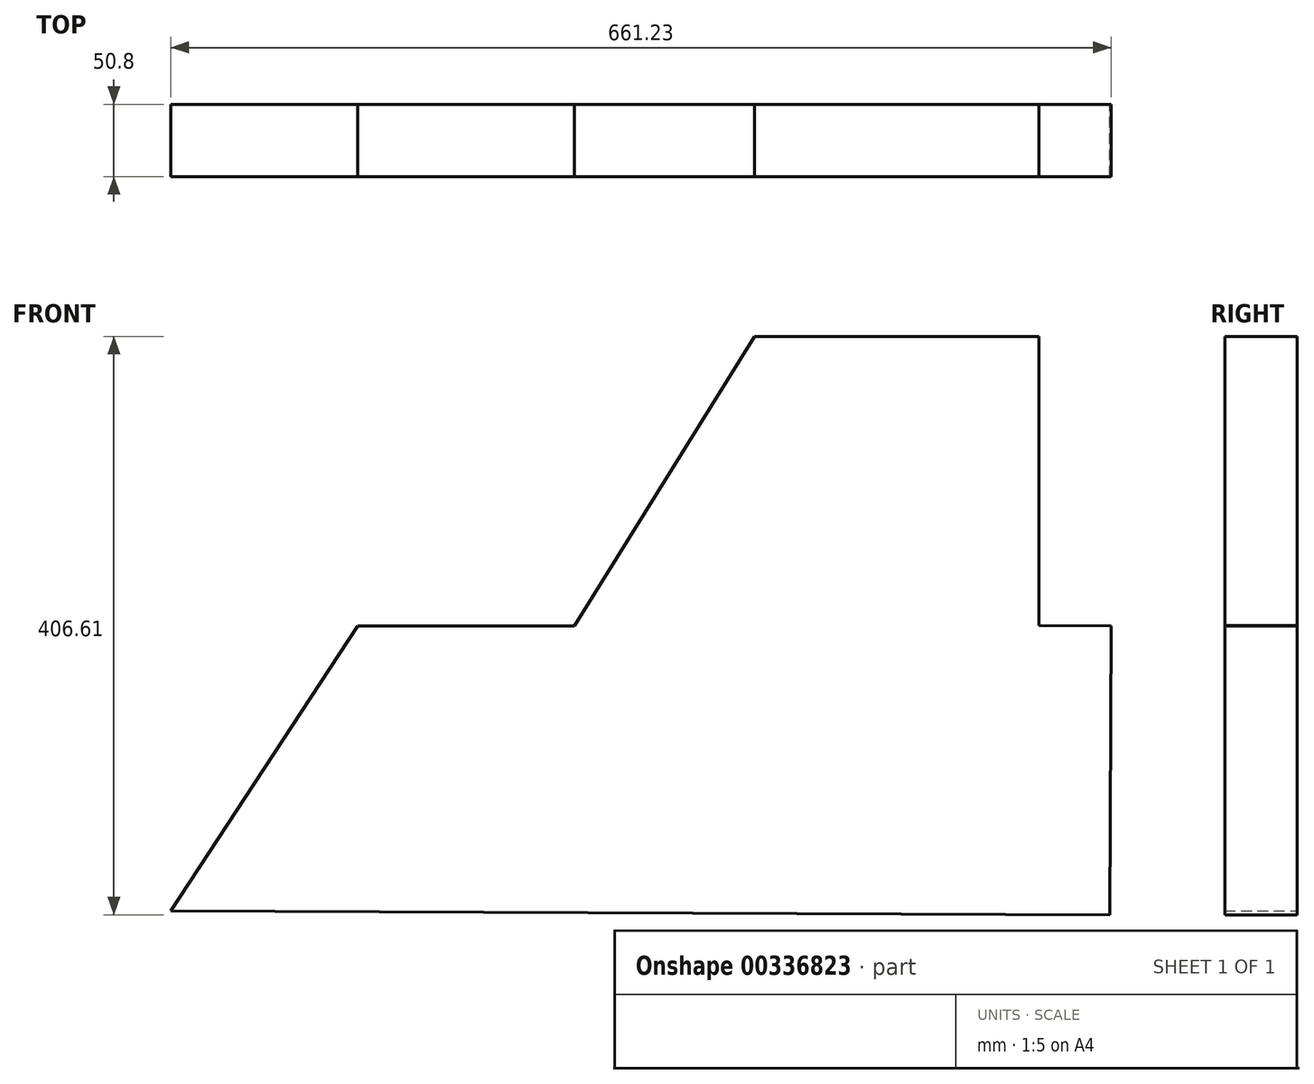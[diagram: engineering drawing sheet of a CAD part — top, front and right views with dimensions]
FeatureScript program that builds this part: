
annotation { "Feature Type Name" : "Feature", "Feature Type Description" : "" }
export const myFeature = defineFeature(function(context is Context, id is Id, definition is map)
    precondition{}
    {
        {
            var Q0;
            Q0=qCreatedBy(makeId("Front.planeOp"),FACE);
            var sketch = newSketch(context, id + "F0", { "sketchPlane" : qUnion([Q0])});
            skLineSegment(sketch, "E0", {"start": v(278.88, 203.4) * mm, "end": v(75.68, 203.4) * mm});
            skLineSegment(sketch, "E1", {"start": v(75.68, 203.4) * mm, "end": v(-50.98, 0) * mm});
            skLineSegment(sketch, "E2", {"start": v(-50.98, 0) * mm, "end": v(-203.38, 0) * mm});
            skLineSegment(sketch, "E3", {"start": v(-203.38, 0) * mm, "end": v(-334.65, -200.47) * mm});
            skLineSegment(sketch, "E4", {"start": v(-334.65, -200.47) * mm, "end": v(325.74, -203.2) * mm});
            skLineSegment(sketch, "E5", {"start": v(325.74, -203.2) * mm, "end": v(326.58, 0) * mm});
            skLineSegment(sketch, "E6", {"start": v(326.58, 0) * mm, "end": v(275.78, 0.2) * mm});
            skLineSegment(sketch, "E7", {"start": v(275.78, 0.2) * mm, "end": v(275.78, 203.4) * mm});
            skLineSegment(sketch, "E8", {"start": v(278.88, 203.4) * mm, "end": v(275.78, 203.4) * mm});
            skSolve(sketch);
        }
        {
            var Q0;
            Q0=makeQuery(id+"F0.imprint","IMPRINT",FACE,{"disambiguationData":[TD([[makeQuery(id+"F0.imprint","IMPRINT",EDGE,{"derivedFrom":sQuery(id+"F0.wireOp",EDGE,"E0")}),1.0]])]});
            extrude(context, id + "F1", {"entities" : qUnion([Q0]), "depth" : 50.8 * mm});
        }
    });
